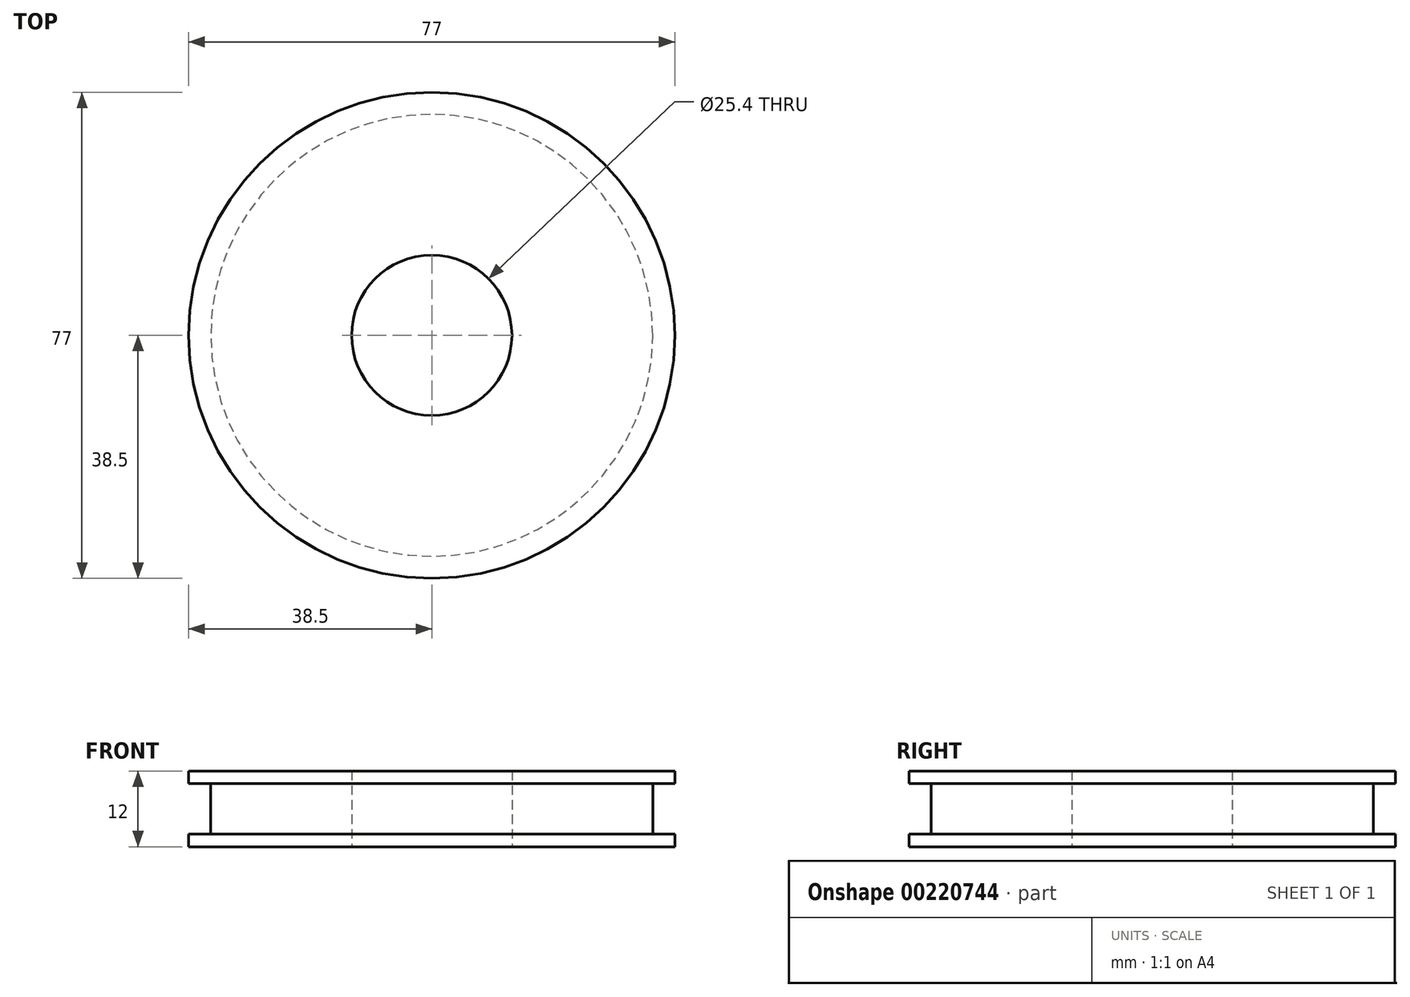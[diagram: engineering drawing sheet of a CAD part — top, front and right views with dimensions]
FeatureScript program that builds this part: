
annotation { "Feature Type Name" : "Feature", "Feature Type Description" : "" }
export const myFeature = defineFeature(function(context is Context, id is Id, definition is map)
    precondition{}
    {
        {
            var Q0;
            Q0=qCreatedBy(makeId("Top.planeOp"),FACE);
            var sketch = newSketch(context, id + "F0", { "sketchPlane" : qUnion([Q0])});
            skCircle(sketch, "E0", {"center": v(0, 0) * mm, "radius": 35 * mm});
            skCircle(sketch, "E1", {"center": v(0, 0) * mm, "radius": 38.5 * mm});
            skCircle(sketch, "E2", {"center": v(0, 0) * mm, "radius": 12.7 * mm});
            skSolve(sketch);
        }
        {
            var Q0;
            Q0=makeQuery(id+"F0.imprint","IMPRINT",FACE,{"disambiguationData":[TD([[makeQuery(id+"F0.imprint","IMPRINT",EDGE,{"derivedFrom":sQuery(id+"F0.wireOp",EDGE,"E0")}),-1.0]])]});
            var Q1;
            Q1=makeQuery(id+"F0.imprint","IMPRINT",FACE,{"disambiguationData":[TD([[makeQuery(id+"F0.imprint","IMPRINT",EDGE,{"derivedFrom":sQuery(id+"F0.wireOp",EDGE,"E0")}),1.0]])]});
            extrude(context, id + "F1", {"entities" : qUnion([Q0, Q1]), "depth" : 2 * mm});
        }
        {
            var Q0;
            Q0=makeQuery(id+"F0.imprint","IMPRINT",FACE,{"disambiguationData":[TD([[makeQuery(id+"F0.imprint","IMPRINT",EDGE,{"derivedFrom":sQuery(id+"F0.wireOp",EDGE,"E0")}),1.0]])]});
            extrude(context, id + "F2", {"entities" : qUnion([Q0]), "operationType" : NewBodyOperationType.ADD, "depth" : 10 * mm});
        }
        {
            var Q0;
            Q0=makeQuery(id+"F2.opExtrude","CAP_FACE",FACE,{"disambiguationData":[OSD([sQuery(id+"F0.wireOp",EDGE,"E0"),sQuery(id+"F0.wireOp",EDGE,"E2")])],"isStart":false});
            var sketch = newSketch(context, id + "F3", { "sketchPlane" : qUnion([Q0])});
            skCircle(sketch, "E3", {"center": v(0, 0) * mm, "radius": 38.5 * mm});
            skSolve(sketch);
        }
        {
            var Q0;
            Q0=makeQuery(id+"F3.imprint","IMPRINT",FACE,{"disambiguationData":[TD([[makeQuery(id+"F3.imprint","IMPRINT",EDGE,{"derivedFrom":makeQuery(id+"F2.opExtrude","CAP_EDGE",EDGE,{"disambiguationData":[OSD([sQuery(id+"F0.wireOp",EDGE,"E0")])],"isStart":false})}),1.0]])]});
            var Q1;
            Q1=makeQuery(id+"F3.imprint","IMPRINT",FACE,{"disambiguationData":[TD([[makeQuery(id+"F3.imprint","IMPRINT",EDGE,{"derivedFrom":sQuery(id+"F3.wireOp",EDGE,"E3")}),1.0]])]});
            extrude(context, id + "F4", {"entities" : qUnion([Q0, Q1]), "operationType" : NewBodyOperationType.ADD, "depth" : 2 * mm});
        }
    });
